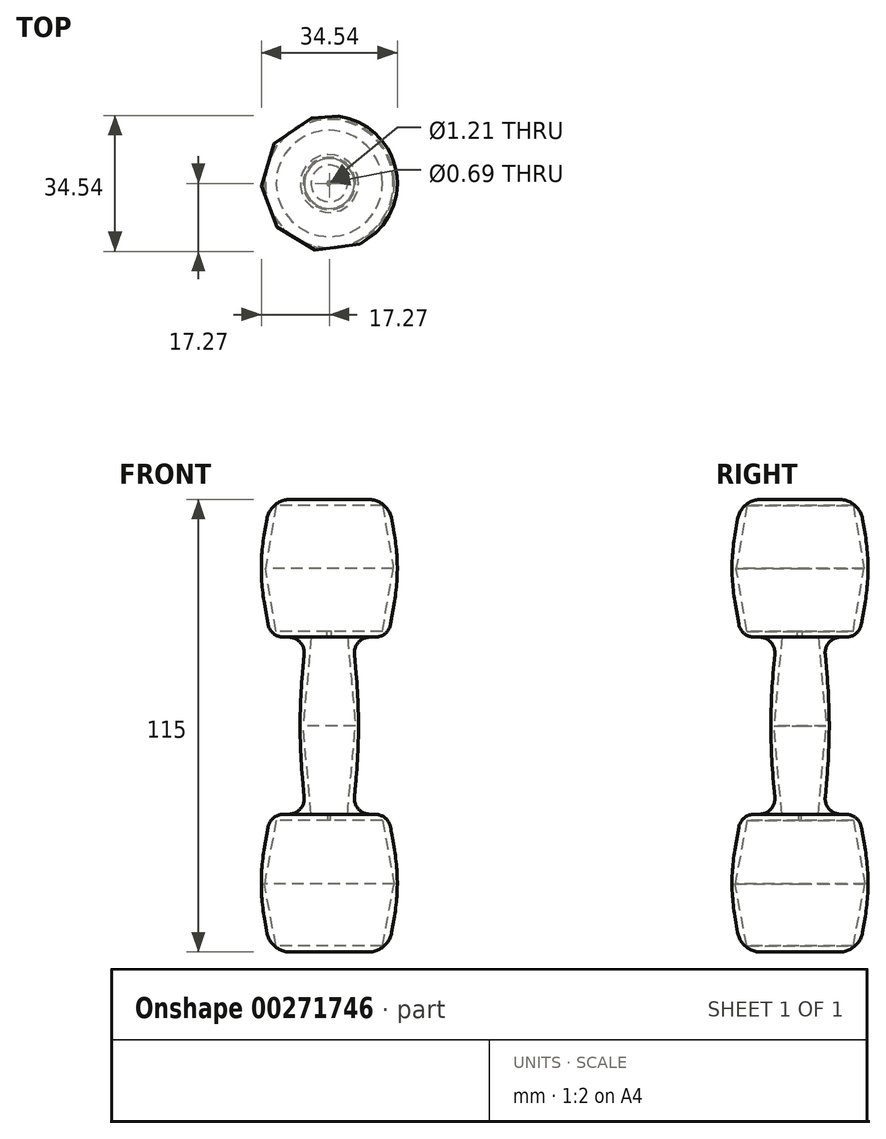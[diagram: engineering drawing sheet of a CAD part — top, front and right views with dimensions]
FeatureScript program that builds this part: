
annotation { "Feature Type Name" : "Feature", "Feature Type Description" : "" }
export const myFeature = defineFeature(function(context is Context, id is Id, definition is map)
    precondition{}
    {
        {
            var Q0;
            Q0=qCreatedBy(makeId("Front.planeOp"),FACE);
            var sketch = newSketch(context, id + "F0", { "sketchPlane" : qUnion([Q0])});
            skLineSegment(sketch, "E0", {"start": v(0, 57.5) * mm, "end": v(15, 57.5) * mm});
            skLineSegment(sketch, "E1", {"start": v(15, 22.5) * mm, "end": v(6, 22.5) * mm});
            skLineSegment(sketch, "E2", {"start": v(6, -22.5) * mm, "end": v(15, -22.5) * mm});
            skLineSegment(sketch, "E3", {"start": v(15, -57.5) * mm, "end": v(0, -57.5) * mm});
            skLineSegment(sketch, "E4", {"start": v(0, 56) * mm, "end": v(13.5, 56) * mm});
            skLineSegment(sketch, "E5", {"start": v(13.5, 24) * mm, "end": v(4.5, 24) * mm});
            skLineSegment(sketch, "E6", {"start": v(4.5, -24) * mm, "end": v(13.5, -24) * mm});
            skLineSegment(sketch, "E7", {"start": v(13.5, -56) * mm, "end": v(0, -56) * mm});
            skLineSegment(sketch, "E8", {"start": v(0, -56) * mm, "end": v(0, -57.5) * mm});
            skLineSegment(sketch, "E9", {"start": v(0, 56) * mm, "end": v(0, 57.5) * mm});
            skLineSegment(sketch, "E10", {"start": v(0, 73.07) * mm, "end": v(0, 60.25) * mm});
            skLineSegment(sketch, "E11", {"start": v(15, 57.5) * mm, "end": v(18, 40) * mm});
            skLineSegment(sketch, "E12", {"start": v(18, 40) * mm, "end": v(15, 22.5) * mm});
            skLineSegment(sketch, "E13", {"start": v(15, -22.5) * mm, "end": v(18, -40) * mm});
            skLineSegment(sketch, "E14", {"start": v(18, -40) * mm, "end": v(15, -57.5) * mm});
            skLineSegment(sketch, "E15", {"start": v(13.5, 56) * mm, "end": v(16.24, 40) * mm});
            skLineSegment(sketch, "E16", {"start": v(16.24, 40) * mm, "end": v(13.5, 24) * mm});
            skLineSegment(sketch, "E17", {"start": v(13.5, -24) * mm, "end": v(16.5, -40.18) * mm});
            skLineSegment(sketch, "E18", {"start": v(16.5, -40.18) * mm, "end": v(13.5, -56) * mm});
            skLineSegment(sketch, "E19", {"start": v(6, 22.5) * mm, "end": v(8, 0) * mm});
            skLineSegment(sketch, "E20", {"start": v(8, 0) * mm, "end": v(6, -22.5) * mm});
            skLineSegment(sketch, "E21", {"start": v(4.63, 22.5) * mm, "end": v(6.63, 0) * mm});
            skLineSegment(sketch, "E22", {"start": v(6.63, 0) * mm, "end": v(4.63, -22.5) * mm});
            skLineSegment(sketch, "E23", {"start": v(4.5, 24) * mm, "end": v(0.6, 24) * mm});
            skLineSegment(sketch, "E24", {"start": v(0.6, 24) * mm, "end": v(0.6, 22.5) * mm});
            skLineSegment(sketch, "E25", {"start": v(0.6, 22.5) * mm, "end": v(4.63, 22.5) * mm});
            skLineSegment(sketch, "E26", {"start": v(4.5, -24) * mm, "end": v(0.35, -24) * mm});
            skLineSegment(sketch, "E27", {"start": v(0.35, -24) * mm, "end": v(0.35, -22.5) * mm});
            skLineSegment(sketch, "E28", {"start": v(0.35, -22.5) * mm, "end": v(4.63, -22.5) * mm});
            skSolve(sketch);
        }
        {
            var Q0;
            Q0=makeQuery(id+"F0.imprint","IMPRINT",FACE,{"disambiguationData":[TD([[makeQuery(id+"F0.imprint","IMPRINT",EDGE,{"derivedFrom":sQuery(id+"F0.wireOp",EDGE,"E0")}),-1.0]])]});
            var Q1;
            Q1=sQuery(id+"F0.wireOp",EDGE,"E10");
            revolve(context, id + "F1", {"entities" : qUnion([Q0]), "axis" : qUnion([Q1]), "revolveType" : RevolveType.FULL});
        }
        {
            var Q0;
            Q0=makeQuery(id+"F1.opRevolve","SWEPT_EDGE",EDGE,{"disambiguationData":[OSD([sQuery(id+"F0.wireOp",EDGE,"R9cUdnq8-hsG9-EXji-MXBi-fj2GTfEwhy8Y"),sQuery(id+"F0.wireOp",EDGE,"E2")])]});
            var Q1;
            Q1=makeQuery(id+"F1.opRevolve","SWEPT_EDGE",EDGE,{"disambiguationData":[OSD([sQuery(id+"F0.wireOp",EDGE,"E1"),sQuery(id+"F0.wireOp",EDGE,"R9cUdnq8-hsG9-EXji-MXBi-fj2GTfEwhy8Y")])]});
            fillet(context, id + "F2", {"entities" : qUnion([Q0, Q1]), "radius" : 4 * mm, "tangentPropagation" : true, "allowEdgeOverflow" : false});
        }
        {
            var Q0;
            Q0=makeQuery(id+"F1.opRevolve","SWEPT_EDGE",EDGE,{"disambiguationData":[OSD([sQuery(id+"F0.wireOp",EDGE,"E11"),sQuery(id+"F0.wireOp",EDGE,"E12")])]});
            var Q1;
            Q1=makeQuery(id+"F1.opRevolve","SWEPT_EDGE",EDGE,{"disambiguationData":[OSD([sQuery(id+"F0.wireOp",EDGE,"E13"),sQuery(id+"F0.wireOp",EDGE,"E14")])]});
            fillet(context, id + "F3", {"entities" : qUnion([Q0, Q1]), "radius" : 50 * mm, "tangentPropagation" : true, "allowEdgeOverflow" : false});
        }
        {
            var Q0;
            Q0=makeQuery(id+"F1.opRevolve","SWEPT_EDGE",EDGE,{"disambiguationData":[OSD([sQuery(id+"F0.wireOp",EDGE,"E0"),sQuery(id+"F0.wireOp",EDGE,"E11")])]});
            var Q1;
            Q1=makeQuery(id+"F1.opRevolve","SWEPT_EDGE",EDGE,{"disambiguationData":[OSD([sQuery(id+"F0.wireOp",EDGE,"E2"),sQuery(id+"F0.wireOp",EDGE,"E13")])]});
            var Q2;
            Q2=makeQuery(id+"F1.opRevolve","SWEPT_EDGE",EDGE,{"disambiguationData":[OSD([sQuery(id+"F0.wireOp",EDGE,"E1"),sQuery(id+"F0.wireOp",EDGE,"E12")])]});
            var Q3;
            Q3=makeQuery(id+"F1.opRevolve","SWEPT_EDGE",EDGE,{"disambiguationData":[OSD([sQuery(id+"F0.wireOp",EDGE,"E3"),sQuery(id+"F0.wireOp",EDGE,"E14")])]});
            fillet(context, id + "F4", {"entities" : qUnion([Q0, Q1, Q2, Q3]), "radius" : 6 * mm, "tangentPropagation" : true, "allowEdgeOverflow" : false});
        }
        {
            var Q0;
            Q0=makeQuery(id+"F1.opRevolve","SWEPT_EDGE",EDGE,{"disambiguationData":[OSD([sQuery(id+"F0.wireOp",EDGE,"E19"),sQuery(id+"F0.wireOp",EDGE,"E20")])]});
            fillet(context, id + "F5", {"entities" : qUnion([Q0]), "radius" : 150 * mm, "tangentPropagation" : true, "allowEdgeOverflow" : false});
        }
    });
